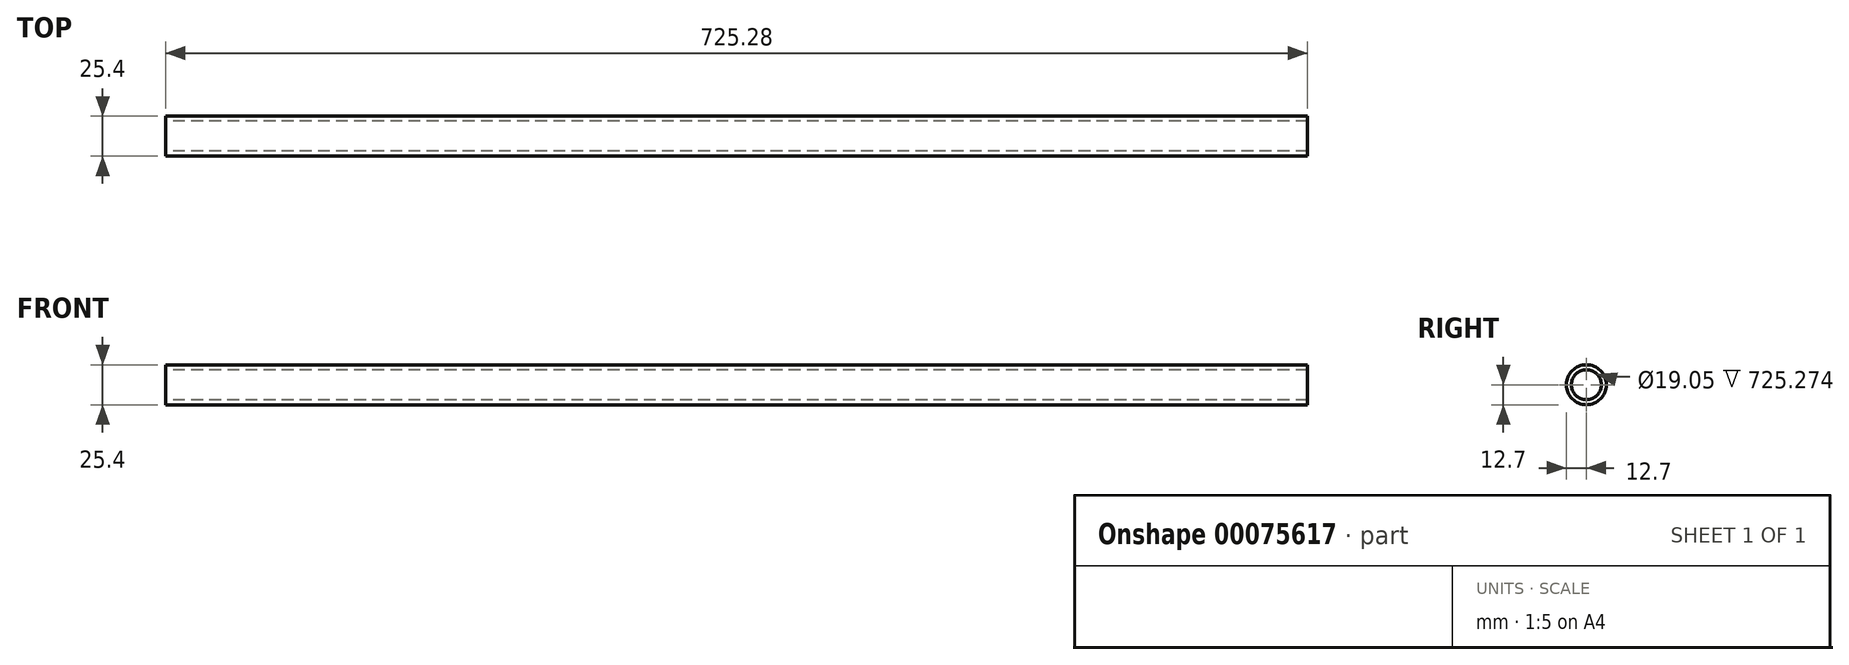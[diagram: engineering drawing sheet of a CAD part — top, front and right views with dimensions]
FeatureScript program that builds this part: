
annotation { "Feature Type Name" : "Feature", "Feature Type Description" : "" }
export const myFeature = defineFeature(function(context is Context, id is Id, definition is map)
    precondition{}
    {
        {
            var Q0;
            Q0=qCreatedBy(makeId("Right.planeOp"),FACE);
            var sketch = newSketch(context, id + "F0", { "sketchPlane" : qUnion([Q0])});
            skCircle(sketch, "E0", {"center": v(0, 0) * mm, "radius": 12.7 * mm});
            skSolve(sketch);
        }
        {
            var Q0;
            Q0=makeQuery(id+"F0.imprint","IMPRINT",FACE,{"disambiguationData":[TD([[makeQuery(id+"F0.imprint","IMPRINT",EDGE,{"derivedFrom":sQuery(id+"F0.wireOp",EDGE,"E0")}),1.0]])]});
            var sketch = newSketch(context, id + "F1", { "sketchPlane" : qUnion([Q0])});
            skCircle(sketch, "E1", {"center": v(0, 0) * mm, "radius": 9.52 * mm});
            skSolve(sketch);
        }
        {
            var Q0;
            Q0=makeQuery(id+"F0.imprint","IMPRINT",FACE,{"disambiguationData":[TD([[makeQuery(id+"F0.imprint","IMPRINT",EDGE,{"derivedFrom":sQuery(id+"F0.wireOp",EDGE,"E0")}),1.0]])]});
            extrude(context, id + "F2", {"entities" : qUnion([Q0]), "depth" : 362.64 * mm});
        }
        {
            var Q0;
            Q0=sQuery(id+"F1.wireOp",VERTEX,"E1.center");
            var Q1;
            Q1=makeQuery(id+"F2.opExtrude","SWEPT_BODY",BODY,{"disambiguationData":[OSD([sQuery(id+"F0.wireOp",EDGE,"E0")])]});
            hole(context, id + "F3", {"style" : HoleStyle.SIMPLE, "endStyle" : HoleEndStyle.THROUGH, "oppositeDirection" : true, "holeDiameter" : 19.05 * mm, "locations" : qUnion([Q0]), "scope" : qUnion([Q1]), "isTappedThrough" : true});
        }
        {
            var Q0;
            Q0=makeQuery(id+"F2.opExtrude","SWEPT_BODY",BODY,{"disambiguationData":[OSD([sQuery(id+"F0.wireOp",EDGE,"E0")])]});
            var Q1;
            Q1=qCreatedBy(makeId("Right.planeOp"),FACE);
            mirror(context, id + "F4", {"operationType" : NewBodyOperationType.ADD, "entities" : qUnion([Q0]), "mirrorPlane" : qUnion([Q1])});
        }
    });
